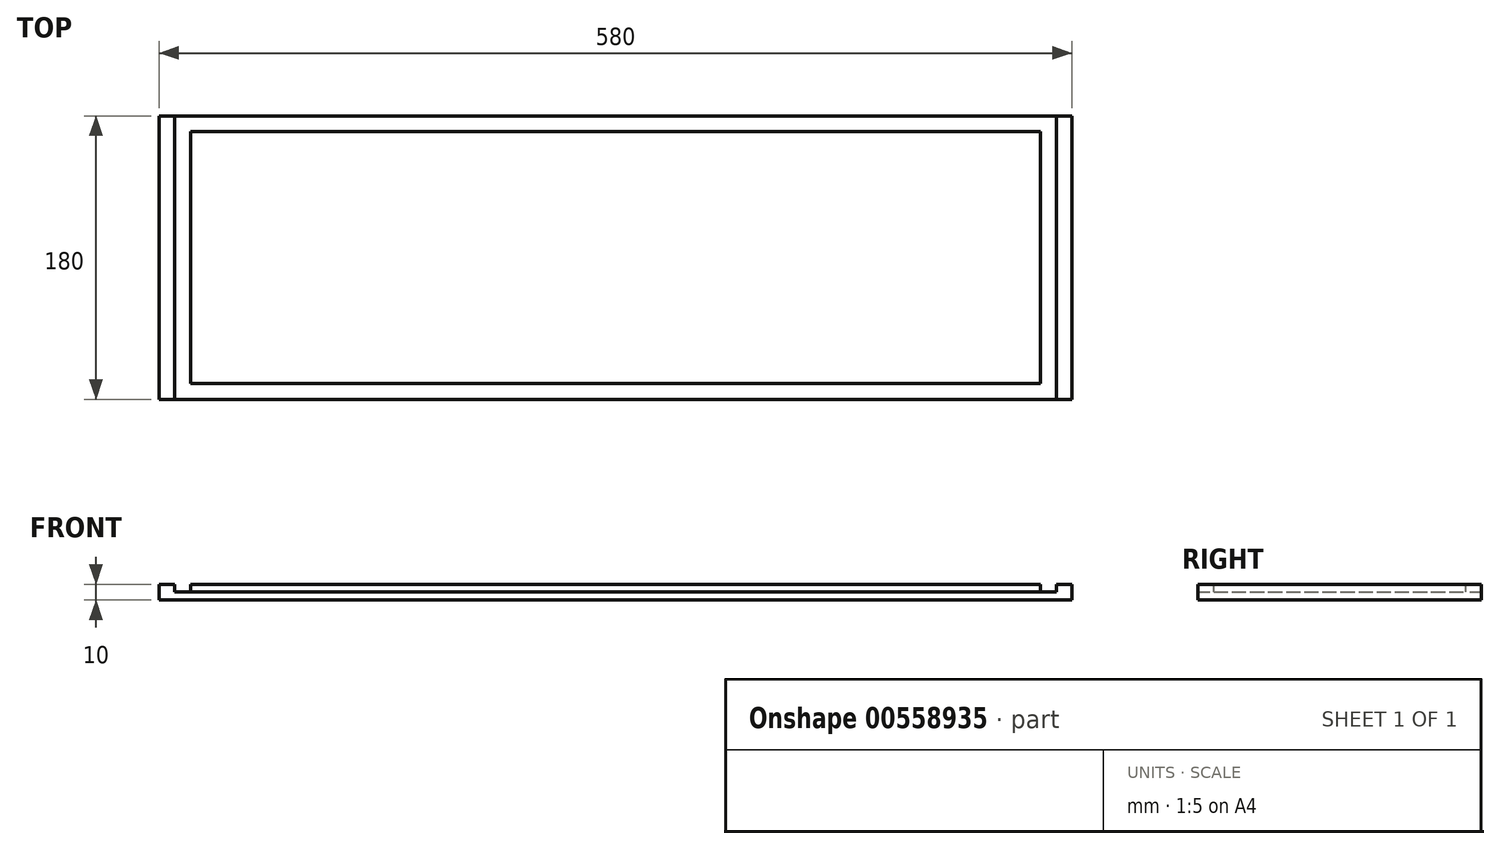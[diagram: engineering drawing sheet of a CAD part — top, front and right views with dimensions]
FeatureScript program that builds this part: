
annotation { "Feature Type Name" : "Feature", "Feature Type Description" : "" }
export const myFeature = defineFeature(function(context is Context, id is Id, definition is map)
    precondition{}
    {
        {
            var Q0;
            Q0=qCreatedBy(makeId("Top.planeOp"),FACE);
            var sketch = newSketch(context, id + "F0", { "sketchPlane" : qUnion([Q0])});
            skLineSegment(sketch, "E0.bottom", {"start": v(290, -90) * mm, "end": v(-290, -90) * mm});
            skLineSegment(sketch, "E0.top", {"start": v(290, 90) * mm, "end": v(-290, 90) * mm});
            skLineSegment(sketch, "E0.left", {"start": v(290, -90) * mm, "end": v(290, 90) * mm});
            skLineSegment(sketch, "E0.right", {"start": v(-290, -90) * mm, "end": v(-290, 90) * mm});
            skPoint(sketch, "E0.middle", {"position": v(0, 0) * mm});
            skSolve(sketch);
        }
        {
            var Q0;
            Q0=makeQuery(id+"F0.imprint","IMPRINT",FACE,{"disambiguationData":[TD([[makeQuery(id+"F0.imprint","IMPRINT",EDGE,{"derivedFrom":sQuery(id+"F0.wireOp",EDGE,"E0.bottom")}),-1.0]])]});
            extrude(context, id + "F1", {"entities" : qUnion([Q0]), "depth" : 10 * mm, "offsetDistance" : 25 * mm});
        }
        {
            var Q0;
            Q0=makeQuery(id+"F1.opExtrude","CAP_FACE",FACE,{"disambiguationData":[OSD([sQuery(id+"F0.wireOp",EDGE,"E0.bottom"),sQuery(id+"F0.wireOp",EDGE,"E0.top"),sQuery(id+"F0.wireOp",EDGE,"E0.left"),sQuery(id+"F0.wireOp",EDGE,"E0.right")])],"isStart":false});
            var sketch = newSketch(context, id + "F2", { "sketchPlane" : qUnion([Q0])});
            skLineSegment(sketch, "E1.bottom", {"start": v(280, -90) * mm, "end": v(-280, -90) * mm});
            skLineSegment(sketch, "E1.top", {"start": v(280, 90) * mm, "end": v(-280, 90) * mm});
            skLineSegment(sketch, "E1.left", {"start": v(280, -90) * mm, "end": v(280, 90) * mm});
            skLineSegment(sketch, "E1.right", {"start": v(-280, -90) * mm, "end": v(-280, 90) * mm});
            skPoint(sketch, "E1.middle", {"position": v(0, 0) * mm});
            skLineSegment(sketch, "E2.bottom", {"start": v(270, -80) * mm, "end": v(-270, -80) * mm});
            skLineSegment(sketch, "E2.top", {"start": v(270, 80) * mm, "end": v(-270, 80) * mm});
            skLineSegment(sketch, "E2.left", {"start": v(270, -80) * mm, "end": v(270, 80) * mm});
            skLineSegment(sketch, "E2.right", {"start": v(-270, -80) * mm, "end": v(-270, 80) * mm});
            skSolve(sketch);
        }
        {
            var Q0;
            Q0 = qSketchRegion(id + "F2", true);
            extrude(context, id + "F3", {"entities" : qUnion([Q0]), "operationType" : NewBodyOperationType.REMOVE, "oppositeDirection" : true, "depth" : 5 * mm, "offsetDistance" : 25 * mm});
        }
    });
